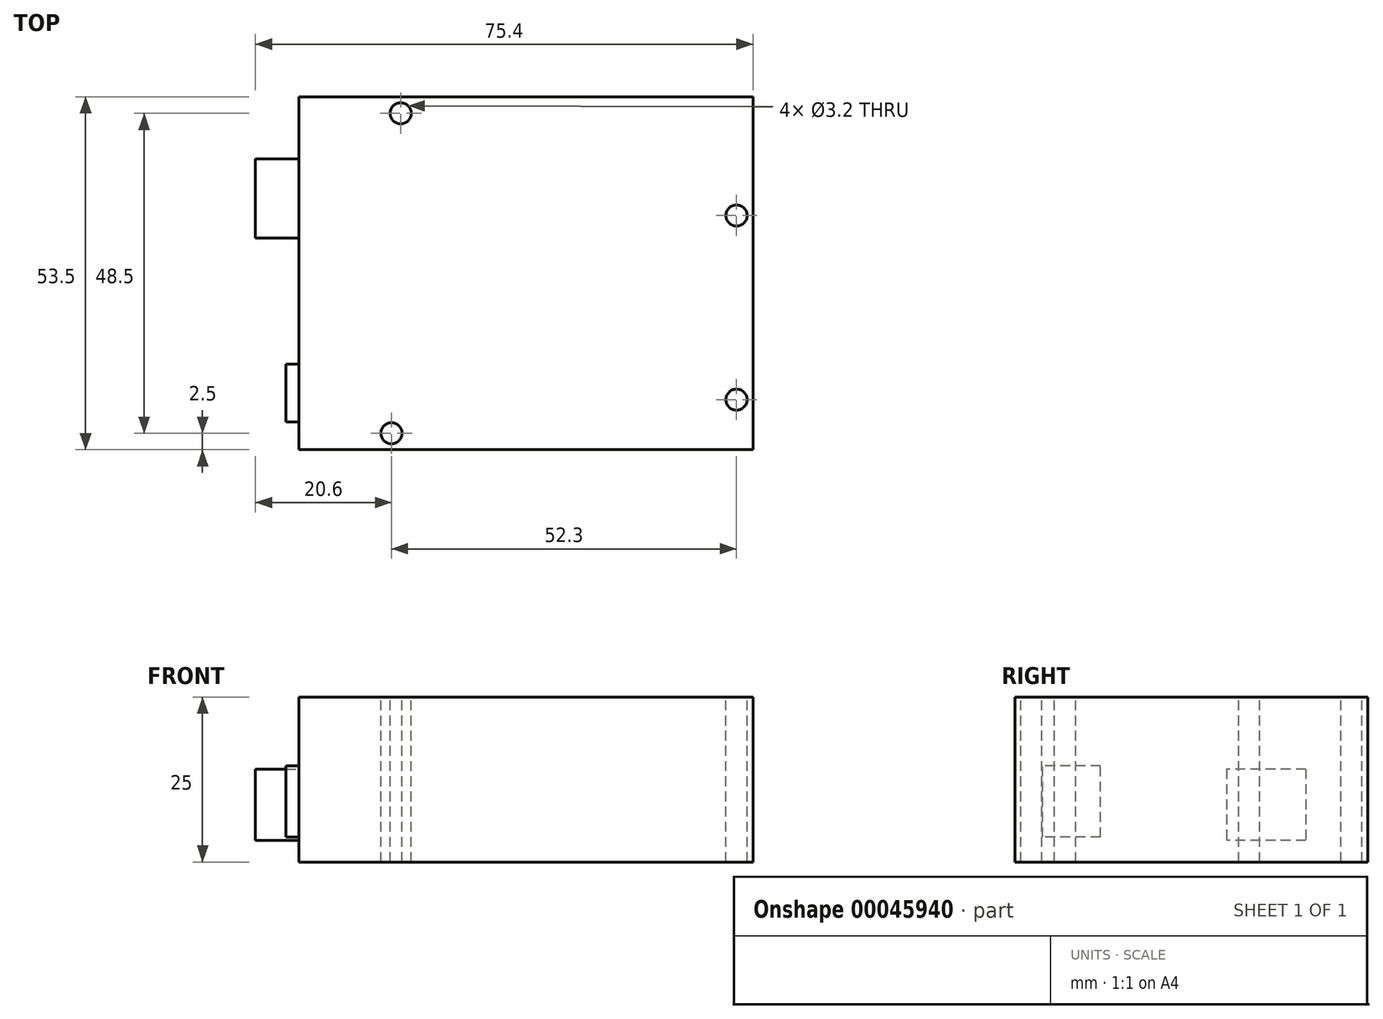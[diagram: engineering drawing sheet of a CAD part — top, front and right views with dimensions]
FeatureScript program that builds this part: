
annotation { "Feature Type Name" : "Feature", "Feature Type Description" : "" }
export const myFeature = defineFeature(function(context is Context, id is Id, definition is map)
    precondition{}
    {
        {
            var Q0;
            Q0=qCreatedBy(makeId("Top.planeOp"),FACE);
            var sketch = newSketch(context, id + "F0", { "sketchPlane" : qUnion([Q0])});
            skLineSegment(sketch, "E0.rect.bottom", {"start": v(34.4, 26.75) * mm, "end": v(-34.4, 26.75) * mm});
            skLineSegment(sketch, "E0.rect.top", {"start": v(34.4, -26.75) * mm, "end": v(-34.4, -26.75) * mm});
            skLineSegment(sketch, "E0.rect.left", {"start": v(34.4, 26.75) * mm, "end": v(34.4, -26.75) * mm});
            skLineSegment(sketch, "E0.rect.right", {"start": v(-34.4, 26.75) * mm, "end": v(-34.4, -26.75) * mm});
            skPoint(sketch, "E0.rect.middle", {"position": v(0, 0) * mm});
            skSolve(sketch);
        }
        {
            var Q0;
            Q0=qSketchRegion(id+"F0",true);
            extrude(context, id + "F1", {"entities" : qUnion([Q0]), "depth" : 25 * mm});
        }
        {
            var Q0;
            Q0=makeQuery(id+"F1.opExtrude","CAP_FACE",FACE,{"disambiguationData":[OSD([sQuery(id+"F0.wireOp",EDGE,"E0.rect.bottom"),sQuery(id+"F0.wireOp",EDGE,"E0.rect.top"),sQuery(id+"F0.wireOp",EDGE,"E0.rect.left"),sQuery(id+"F0.wireOp",EDGE,"E0.rect.right")])],"isStart":false});
            var sketch = newSketch(context, id + "F2", { "sketchPlane" : qUnion([Q0])});
            skCircle(sketch, "E1", {"center": v(-19, 24.25) * mm, "radius": 1.6 * mm});
            skCircle(sketch, "E2", {"center": v(31.9, 8.75) * mm, "radius": 1.6 * mm});
            skCircle(sketch, "E3", {"center": v(-20.4, -24.25) * mm, "radius": 1.6 * mm});
            skCircle(sketch, "E4", {"center": v(31.9, -19.15) * mm, "radius": 1.6 * mm});
            skSolve(sketch);
        }
        {
            var Q0;
            Q0=qSketchRegion(id+"F2",true);
            extrude(context, id + "F3", {"entities" : qUnion([Q0]), "operationType" : NewBodyOperationType.REMOVE, "oppositeDirection" : true, "depth" : 25 * mm});
        }
        {
            var Q0;
            Q0=makeQuery(id+"F1.opExtrude","SWEPT_FACE",FACE,{"disambiguationData":[OSD([sQuery(id+"F0.wireOp",EDGE,"E0.rect.right")])]});
            var sketch = newSketch(context, id + "F4", { "sketchPlane" : qUnion([Q0])});
            skLineSegment(sketch, "E5.bottom", {"start": v(-17.35, 14.1) * mm, "end": v(-5.35, 14.1) * mm});
            skLineSegment(sketch, "E5.top", {"start": v(-17.35, 3.3) * mm, "end": v(-5.35, 3.3) * mm});
            skLineSegment(sketch, "E5.left", {"start": v(-17.35, 14.1) * mm, "end": v(-17.35, 3.3) * mm});
            skLineSegment(sketch, "E5.right", {"start": v(-5.35, 14.1) * mm, "end": v(-5.35, 3.3) * mm});
            skSolve(sketch);
        }
        {
            var Q0;
            Q0=qSketchRegion(id+"F4",true);
            extrude(context, id + "F5", {"entities" : qUnion([Q0]), "operationType" : NewBodyOperationType.ADD, "depth" : 6.6 * mm});
        }
        {
            var Q0;
            Q0=makeQuery(id+"F1.opExtrude","SWEPT_FACE",FACE,{"disambiguationData":[OSD([sQuery(id+"F0.wireOp",EDGE,"E0.rect.right")])]});
            var sketch = newSketch(context, id + "F6", { "sketchPlane" : qUnion([Q0])});
            skLineSegment(sketch, "E6.bottom", {"start": v(13.75, 3.78) * mm, "end": v(22.55, 3.78) * mm});
            skLineSegment(sketch, "E6.top", {"start": v(13.75, 14.58) * mm, "end": v(22.55, 14.58) * mm});
            skLineSegment(sketch, "E6.left", {"start": v(13.75, 3.78) * mm, "end": v(13.75, 14.58) * mm});
            skLineSegment(sketch, "E6.right", {"start": v(22.55, 3.78) * mm, "end": v(22.55, 14.58) * mm});
            skSolve(sketch);
        }
        {
            var Q0;
            Q0=qSketchRegion(id+"F6",true);
            extrude(context, id + "F7", {"entities" : qUnion([Q0]), "operationType" : NewBodyOperationType.ADD, "depth" : 2 * mm});
        }
    });
